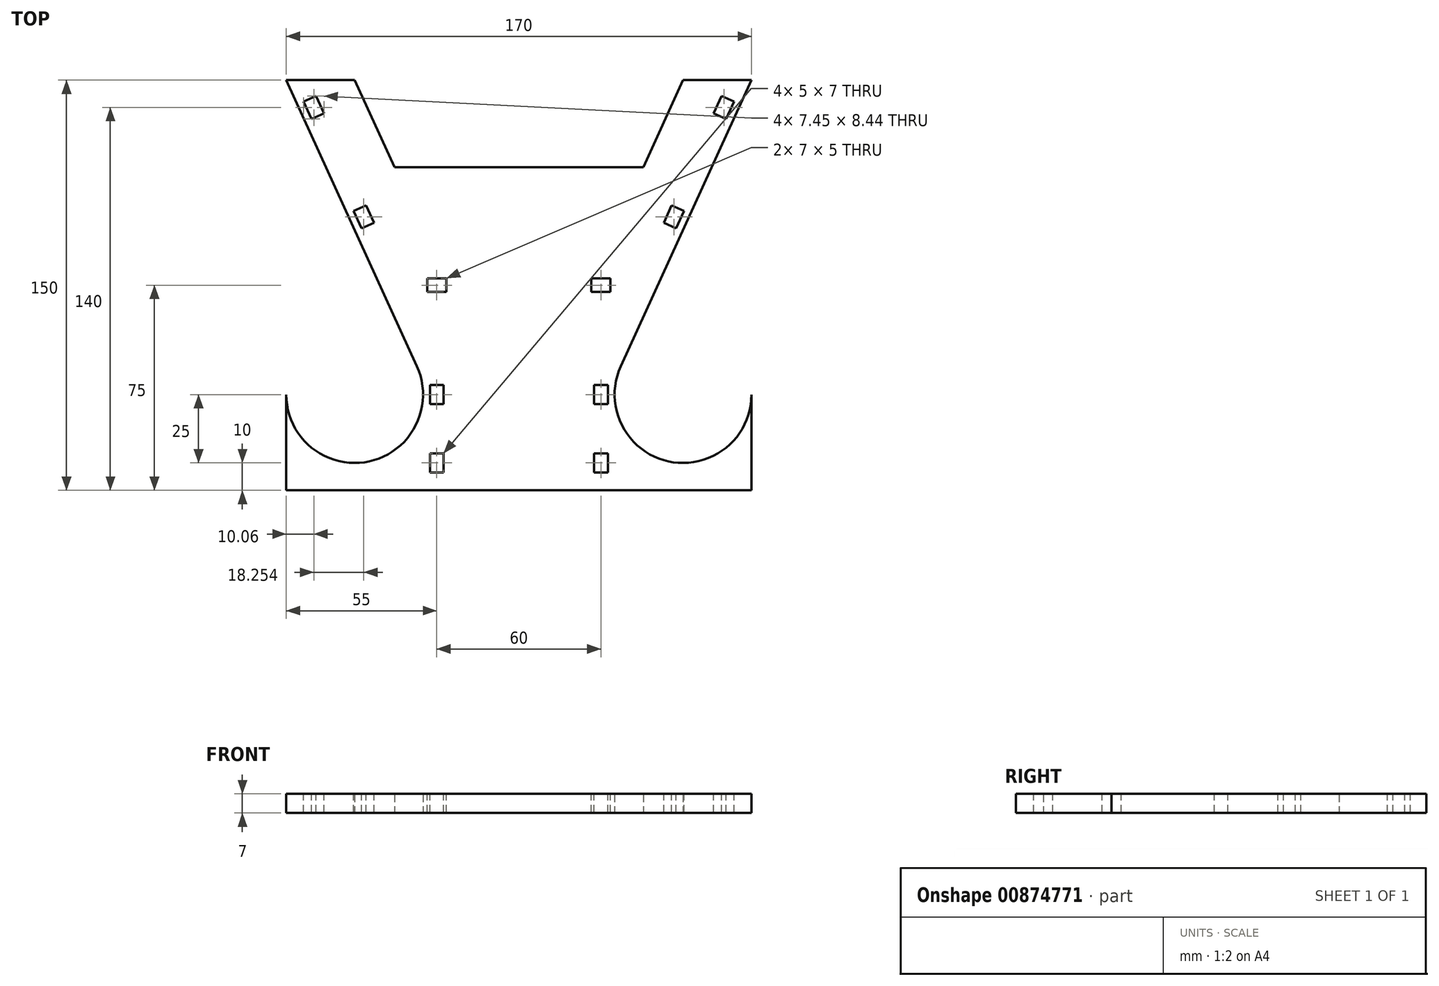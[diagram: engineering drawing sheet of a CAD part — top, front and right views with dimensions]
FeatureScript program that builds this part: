
annotation { "Feature Type Name" : "Feature", "Feature Type Description" : "" }
export const myFeature = defineFeature(function(context is Context, id is Id, definition is map)
    precondition{}
    {
        {
            var Q0;
            Q0=qCreatedBy(makeId("Top.planeOp"),FACE);
            var sketch = newSketch(context, id + "F0", { "sketchPlane" : qUnion([Q0])});
            skLineSegment(sketch, "E0.bottom", {"start": v(85, -75) * mm, "end": v(-85, -75) * mm});
            skLineSegment(sketch, "E0.top", {"start": v(85, 75) * mm, "end": v(-85, 75) * mm});
            skLineSegment(sketch, "E0.left", {"start": v(85, -75) * mm, "end": v(85, 75) * mm});
            skLineSegment(sketch, "E0.right", {"start": v(-85, -75) * mm, "end": v(-85, 75) * mm});
            skPoint(sketch, "E0.middle", {"position": v(0, 0) * mm});
            skLineSegment(sketch, "E1", {"start": v(-60, 75) * mm, "end": v(-60, -75) * mm, "construction": true});
            skLineSegment(sketch, "E2", {"start": v(60, 75) * mm, "end": v(60, -75) * mm, "construction": true});
            skLineSegment(sketch, "E3", {"start": v(-85, -65) * mm, "end": v(85, -65) * mm, "construction": true});
            skPoint(sketch, "E4", {"position": v(-60, -40) * mm});
            skPoint(sketch, "E5", {"position": v(60, -40) * mm});
            skCircle(sketch, "E6", {"center": v(-60, -40) * mm, "radius": 25 * mm});
            skCircle(sketch, "E7", {"center": v(60, -40) * mm, "radius": 25 * mm});
            skLineSegment(sketch, "E8", {"start": v(85, 75) * mm, "end": v(37.26, -29.62) * mm});
            skLineSegment(sketch, "E9", {"start": v(-85, 75) * mm, "end": v(-37.26, -29.62) * mm});
            skLineSegment(sketch, "E10", {"start": v(-60, 75) * mm, "end": v(-45.47, 43.16) * mm});
            skLineSegment(sketch, "E11", {"start": v(60, 75) * mm, "end": v(45.47, 43.16) * mm});
            skLineSegment(sketch, "E12", {"start": v(-45.47, 43.16) * mm, "end": v(45.47, 43.16) * mm});
            skSolve(sketch);
        }
        {
            var Q0;
            {var subQ4=sQuery(id+"F0.wireOp",EDGE,"E0.bottom");Q0=makeQuery(id+"F0.imprint","IMPRINT",FACE,{"disambiguationData":[TD([[makeQuery(id+"F0.imprint","IMPRINT",EDGE,{"derivedFrom":subQ4}),-1.0]])]});}
            extrude(context, id + "F1", {"entities" : qUnion([Q0]), "depth" : 7 * mm, "offsetDistance" : 25 * mm});
        }
        {
            var Q0;
            Q0=makeQuery(id+"F1.opExtrude","CAP_FACE",FACE,{"disambiguationData":[OSD([sQuery(id+"F0.wireOp",EDGE,"E0.bottom"),sQuery(id+"F0.wireOp",EDGE,"E0.top"),sQuery(id+"F0.wireOp",EDGE,"E0.left"),sQuery(id+"F0.wireOp",EDGE,"E0.right"),sQuery(id+"F0.wireOp",EDGE,"E6"),sQuery(id+"F0.wireOp",EDGE,"E7"),sQuery(id+"F0.wireOp",EDGE,"E8"),sQuery(id+"F0.wireOp",EDGE,"E9"),sQuery(id+"F0.wireOp",EDGE,"E10"),sQuery(id+"F0.wireOp",EDGE,"E11"),sQuery(id+"F0.wireOp",EDGE,"E12")])],"isStart":false});
            var sketch = newSketch(context, id + "F2", { "sketchPlane" : qUnion([Q0])});
            skLineSegment(sketch, "E13", {"start": v(0, 43.16) * mm, "end": v(0, -75) * mm, "construction": true});
            skPoint(sketch, "E14", {"position": v(-30, -65) * mm});
            skPoint(sketch, "E15", {"position": v(30, -65) * mm});
            skPoint(sketch, "E16", {"position": v(30, -40) * mm});
            skPoint(sketch, "E17", {"position": v(-30, -40) * mm});
            skPoint(sketch, "E18", {"position": v(-30, 0) * mm});
            skPoint(sketch, "E19", {"position": v(30, 0) * mm});
            skPoint(sketch, "E20", {"position": v(52.98, 15.77) * mm});
            skPoint(sketch, "E21", {"position": v(77.21, 65.96) * mm});
            skPoint(sketch, "E22", {"position": v(-77.4, 65.96) * mm});
            skPoint(sketch, "E23", {"position": v(-52.6, 16.35) * mm});
            skLineSegment(sketch, "E24.bottom", {"start": v(-27.5, -68.5) * mm, "end": v(-32.5, -68.5) * mm});
            skLineSegment(sketch, "E24.top", {"start": v(-27.5, -61.5) * mm, "end": v(-32.5, -61.5) * mm});
            skLineSegment(sketch, "E24.left", {"start": v(-27.5, -68.5) * mm, "end": v(-27.5, -61.5) * mm});
            skLineSegment(sketch, "E24.right", {"start": v(-32.5, -68.5) * mm, "end": v(-32.5, -61.5) * mm});
            skLineSegment(sketch, "E25.bottom", {"start": v(32.5, -68.5) * mm, "end": v(27.5, -68.5) * mm});
            skLineSegment(sketch, "E25.top", {"start": v(32.5, -61.5) * mm, "end": v(27.5, -61.5) * mm});
            skLineSegment(sketch, "E25.left", {"start": v(32.5, -68.5) * mm, "end": v(32.5, -61.5) * mm});
            skLineSegment(sketch, "E25.right", {"start": v(27.5, -68.5) * mm, "end": v(27.5, -61.5) * mm});
            skLineSegment(sketch, "E26.bottom", {"start": v(-27.5, -43.5) * mm, "end": v(-32.5, -43.5) * mm});
            skLineSegment(sketch, "E26.top", {"start": v(-27.5, -36.5) * mm, "end": v(-32.5, -36.5) * mm});
            skLineSegment(sketch, "E26.left", {"start": v(-27.5, -43.5) * mm, "end": v(-27.5, -36.5) * mm});
            skLineSegment(sketch, "E26.right", {"start": v(-32.5, -43.5) * mm, "end": v(-32.5, -36.5) * mm});
            skLineSegment(sketch, "E27.bottom", {"start": v(32.5, -43.5) * mm, "end": v(27.5, -43.5) * mm});
            skLineSegment(sketch, "E27.top", {"start": v(32.5, -36.5) * mm, "end": v(27.5, -36.5) * mm});
            skLineSegment(sketch, "E27.left", {"start": v(32.5, -43.5) * mm, "end": v(32.5, -36.5) * mm});
            skLineSegment(sketch, "E27.right", {"start": v(27.5, -43.5) * mm, "end": v(27.5, -36.5) * mm});
            skLineSegment(sketch, "E28.bottom", {"start": v(-26.5, -2.5) * mm, "end": v(-33.5, -2.5) * mm});
            skLineSegment(sketch, "E28.top", {"start": v(-26.5, 2.5) * mm, "end": v(-33.5, 2.5) * mm});
            skLineSegment(sketch, "E28.left", {"start": v(-26.5, -2.5) * mm, "end": v(-26.5, 2.5) * mm});
            skLineSegment(sketch, "E28.right", {"start": v(-33.5, -2.5) * mm, "end": v(-33.5, 2.5) * mm});
            skLineSegment(sketch, "E29.bottom", {"start": v(33.5, -2.5) * mm, "end": v(26.5, -2.5) * mm});
            skLineSegment(sketch, "E29.top", {"start": v(33.5, 2.5) * mm, "end": v(26.5, 2.5) * mm});
            skLineSegment(sketch, "E29.left", {"start": v(33.5, -2.5) * mm, "end": v(33.5, 2.5) * mm});
            skLineSegment(sketch, "E29.right", {"start": v(26.5, -2.5) * mm, "end": v(26.5, 2.5) * mm});
            skSolve(sketch);
        }
        {
            var Q0;
            Q0 = qSketchRegion(id + "F2", true);
            extrude(context, id + "F3", {"entities" : qUnion([Q0]), "operationType" : NewBodyOperationType.REMOVE, "endBound" : BoundingType.THROUGH_ALL, "oppositeDirection" : true, "depth" : 25 * mm, "offsetDistance" : 25 * mm});
        }
        {
            var Q0;
            Q0=makeQuery(id+"F1.opExtrude","CAP_FACE",FACE,{"disambiguationData":[OSD([sQuery(id+"F0.wireOp",EDGE,"E0.bottom"),sQuery(id+"F0.wireOp",EDGE,"E0.top"),sQuery(id+"F0.wireOp",EDGE,"E0.left"),sQuery(id+"F0.wireOp",EDGE,"E0.right"),sQuery(id+"F0.wireOp",EDGE,"E6"),sQuery(id+"F0.wireOp",EDGE,"E7"),sQuery(id+"F0.wireOp",EDGE,"E8"),sQuery(id+"F0.wireOp",EDGE,"E9"),sQuery(id+"F0.wireOp",EDGE,"E10"),sQuery(id+"F0.wireOp",EDGE,"E11"),sQuery(id+"F0.wireOp",EDGE,"E12")])],"isStart":false});
            var sketch = newSketch(context, id + "F4", { "sketchPlane" : qUnion([Q0])});
            skPoint(sketch, "E30", {"position": v(74.94, 65) * mm});
            skPoint(sketch, "E31", {"position": v(56.69, 25) * mm});
            skPoint(sketch, "E32", {"position": v(-56.69, 25) * mm});
            skPoint(sketch, "E33", {"position": v(-74.94, 65) * mm});
            skLineSegment(sketch, "E34", {"start": v(-74.94, 65) * mm, "end": v(-56.69, 25) * mm, "construction": true});
            skLineSegment(sketch, "E35", {"start": v(74.94, 65) * mm, "end": v(56.69, 25) * mm, "construction": true});
            skLineSegment(sketch, "E36.bottom", {"start": v(75.76, 60.78) * mm, "end": v(71.21, 62.85) * mm});
            skLineSegment(sketch, "E36.top", {"start": v(78.67, 67.15) * mm, "end": v(74.12, 69.22) * mm});
            skLineSegment(sketch, "E36.left", {"start": v(75.76, 60.78) * mm, "end": v(78.67, 67.15) * mm});
            skLineSegment(sketch, "E36.right", {"start": v(71.21, 62.85) * mm, "end": v(74.12, 69.22) * mm});
            skLineSegment(sketch, "E37.bottom", {"start": v(57.5, 20.78) * mm, "end": v(52.96, 22.85) * mm});
            skLineSegment(sketch, "E37.top", {"start": v(60.41, 27.15) * mm, "end": v(55.87, 29.22) * mm});
            skLineSegment(sketch, "E37.left", {"start": v(57.5, 20.78) * mm, "end": v(60.41, 27.15) * mm});
            skLineSegment(sketch, "E37.right", {"start": v(50.08, 16.55) * mm, "end": v(55.87, 29.22) * mm});
            skLineSegment(sketch, "E38.bottom", {"start": v(-52.96, 22.85) * mm, "end": v(-57.5, 20.78) * mm});
            skLineSegment(sketch, "E38.top", {"start": v(-55.87, 29.22) * mm, "end": v(-60.41, 27.15) * mm});
            skLineSegment(sketch, "E38.left", {"start": v(-52.96, 22.85) * mm, "end": v(-55.87, 29.22) * mm});
            skLineSegment(sketch, "E38.right", {"start": v(-57.5, 20.78) * mm, "end": v(-60.41, 27.15) * mm});
            skLineSegment(sketch, "E39.bottom", {"start": v(-71.21, 62.85) * mm, "end": v(-75.76, 60.78) * mm});
            skLineSegment(sketch, "E39.top", {"start": v(-74.12, 69.22) * mm, "end": v(-78.67, 67.15) * mm});
            skLineSegment(sketch, "E39.left", {"start": v(-71.21, 62.85) * mm, "end": v(-74.12, 69.22) * mm});
            skLineSegment(sketch, "E39.right", {"start": v(-75.76, 60.78) * mm, "end": v(-78.67, 67.15) * mm});
            skSolve(sketch);
        }
        {
            var Q0;
            Q0 = qSketchRegion(id + "F4", true);
            extrude(context, id + "F5", {"entities" : qUnion([Q0]), "operationType" : NewBodyOperationType.REMOVE, "endBound" : BoundingType.THROUGH_ALL, "oppositeDirection" : true, "depth" : 25 * mm, "offsetDistance" : 25 * mm});
        }
    });
